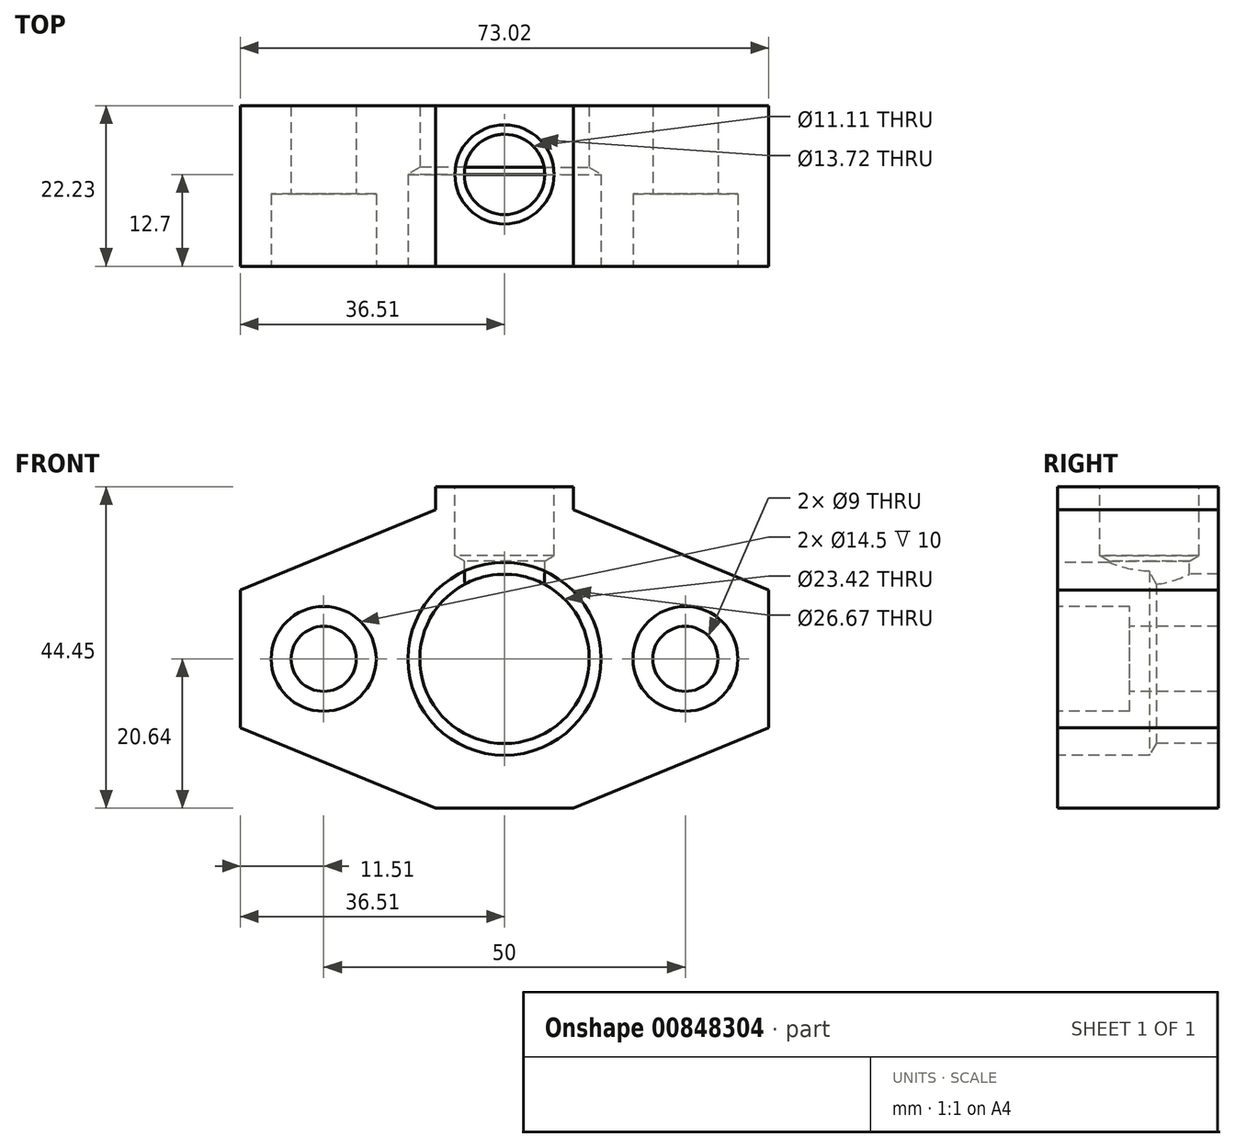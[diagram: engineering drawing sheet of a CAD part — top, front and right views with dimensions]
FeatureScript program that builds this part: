
annotation { "Feature Type Name" : "Feature", "Feature Type Description" : "" }
export const myFeature = defineFeature(function(context is Context, id is Id, definition is map)
    precondition{}
    {
        {
            var Q0;
            Q0=qCreatedBy(makeId("Front.planeOp"),FACE);
            var sketch = newSketch(context, id + "F0", { "sketchPlane" : qUnion([Q0])});
            skLineSegment(sketch, "E0", {"start": v(-36.51, 9.52) * mm, "end": v(-36.51, -9.53) * mm});
            skLineSegment(sketch, "E1", {"start": v(-36.51, -9.53) * mm, "end": v(-9.52, -20.64) * mm});
            skLineSegment(sketch, "E2", {"start": v(-9.52, -20.64) * mm, "end": v(9.52, -20.64) * mm});
            skLineSegment(sketch, "E3", {"start": v(9.52, -20.64) * mm, "end": v(36.51, -9.53) * mm});
            skLineSegment(sketch, "E4", {"start": v(36.51, -9.53) * mm, "end": v(36.51, 9.52) * mm});
            skLineSegment(sketch, "E5", {"start": v(36.51, 9.52) * mm, "end": v(9.52, 20.64) * mm});
            skLineSegment(sketch, "E6", {"start": v(9.52, 20.64) * mm, "end": v(-9.53, 20.64) * mm});
            skLineSegment(sketch, "E7", {"start": v(-9.52, 20.64) * mm, "end": v(-36.51, 9.52) * mm});
            skSolve(sketch);
        }
        {
            var Q0;
            Q0 = qSketchRegion(id + "F0", true);
            extrude(context, id + "F1", {"entities" : qUnion([Q0]), "oppositeDirection" : true, "depth" : 22.22 * mm, "offsetDistance" : 25.4 * mm});
        }
        {
            var Q0;
            Q0=makeQuery(id+"F1.opExtrude","CAP_FACE",FACE,{"disambiguationData":[OSD([sQuery(id+"F0.wireOp",EDGE,"E0"),sQuery(id+"F0.wireOp",EDGE,"E1"),sQuery(id+"F0.wireOp",EDGE,"E2"),sQuery(id+"F0.wireOp",EDGE,"E3"),sQuery(id+"F0.wireOp",EDGE,"E4"),sQuery(id+"F0.wireOp",EDGE,"E5"),sQuery(id+"F0.wireOp",EDGE,"E6"),sQuery(id+"F0.wireOp",EDGE,"E7")])],"isStart":true});
            var sketch = newSketch(context, id + "F2", { "sketchPlane" : qUnion([Q0])});
            skPoint(sketch, "E8", {"position": v(0, 0) * mm});
            skSolve(sketch);
        }
        {
            var Q0;
            Q0=sQuery(id+"F2.wireOp",VERTEX,"E8");
            var Q1;
            Q1=makeQuery(id+"F1.opExtrude","SWEPT_BODY",BODY,{"disambiguationData":[OSD([sQuery(id+"F0.wireOp",EDGE,"E0"),sQuery(id+"F0.wireOp",EDGE,"E1"),sQuery(id+"F0.wireOp",EDGE,"E2"),sQuery(id+"F0.wireOp",EDGE,"E3"),sQuery(id+"F0.wireOp",EDGE,"E4"),sQuery(id+"F0.wireOp",EDGE,"E5"),sQuery(id+"F0.wireOp",EDGE,"E6"),sQuery(id+"F0.wireOp",EDGE,"E7")])]});
            hole(context, id + "F3", {"style" : HoleStyle.SIMPLE, "endStyle" : HoleEndStyle.THROUGH, "holeDiameter" : 23.42 * mm, "majorDiameter" : 6.35 * mm, "isTappedThrough" : true, "tappedDepth" : 12.7 * mm, "tapClearance" : 3, "locations" : qUnion([Q0]), "scope" : qUnion([Q1])});
        }
        {
            var Q0;
            Q0=sQuery(id+"F2.wireOp",VERTEX,"E8");
            var Q1;
            Q1=makeQuery(id+"F1.opExtrude","SWEPT_BODY",BODY,{"disambiguationData":[OSD([sQuery(id+"F0.wireOp",EDGE,"E0"),sQuery(id+"F0.wireOp",EDGE,"E1"),sQuery(id+"F0.wireOp",EDGE,"E2"),sQuery(id+"F0.wireOp",EDGE,"E3"),sQuery(id+"F0.wireOp",EDGE,"E4"),sQuery(id+"F0.wireOp",EDGE,"E5"),sQuery(id+"F0.wireOp",EDGE,"E6"),sQuery(id+"F0.wireOp",EDGE,"E7")])]});
            hole(context, id + "F4", {"style" : HoleStyle.SIMPLE, "endStyle" : HoleEndStyle.BLIND, "holeDiameter" : 26.67 * mm, "majorDiameter" : 19.05 * mm, "holeDepth" : 12.7 * mm, "isTappedThrough" : true, "tappedDepth" : 12.7 * mm, "tapClearance" : 3, "locations" : qUnion([Q0]), "scope" : qUnion([Q1])});
        }
        {
            var Q0;
            Q0=makeQuery(id+"F1.opExtrude","SWEPT_FACE",FACE,{"disambiguationData":[OSD([sQuery(id+"F0.wireOp",EDGE,"E6")])]});
            var sketch = newSketch(context, id + "F5", { "sketchPlane" : qUnion([Q0])});
            skLineSegment(sketch, "E9.0", {"start": v(9.52, 0) * mm, "end": v(-9.53, 0) * mm});
            skLineSegment(sketch, "E10.0", {"start": v(-9.52, 22.23) * mm, "end": v(-9.52, 0) * mm});
            skLineSegment(sketch, "E11.0", {"start": v(9.52, 22.23) * mm, "end": v(-9.52, 22.23) * mm});
            skLineSegment(sketch, "E12.0", {"start": v(9.52, 22.23) * mm, "end": v(9.52, 0) * mm});
            skSolve(sketch);
        }
        {
            var Q0;
            Q0 = qSketchRegion(id + "F5", true);
            extrude(context, id + "F6", {"entities" : qUnion([Q0]), "operationType" : NewBodyOperationType.ADD, "depth" : 3.17 * mm, "offsetDistance" : 25.4 * mm});
        }
        {
            var Q0;
            Q0=makeQuery(id+"F6.opExtrude","CAP_FACE",FACE,{"disambiguationData":[OSD([sQuery(id+"F5.wireOp",EDGE,"E9.0"),sQuery(id+"F5.wireOp",EDGE,"E10.0"),sQuery(id+"F5.wireOp",EDGE,"E11.0"),sQuery(id+"F5.wireOp",EDGE,"E12.0")])],"isStart":false});
            var sketch = newSketch(context, id + "F7", { "sketchPlane" : qUnion([Q0])});
            skPoint(sketch, "E13", {"position": v(0, 12.7) * mm});
            skSolve(sketch);
        }
        {
            var Q0;
            Q0=sQuery(id+"F7.wireOp",VERTEX,"E13");
            var Q1;
            Q1=makeQuery(id+"F1.opExtrude","SWEPT_BODY",BODY,{"disambiguationData":[OSD([sQuery(id+"F0.wireOp",EDGE,"E0"),sQuery(id+"F0.wireOp",EDGE,"E1"),sQuery(id+"F0.wireOp",EDGE,"E2"),sQuery(id+"F0.wireOp",EDGE,"E3"),sQuery(id+"F0.wireOp",EDGE,"E4"),sQuery(id+"F0.wireOp",EDGE,"E5"),sQuery(id+"F0.wireOp",EDGE,"E6"),sQuery(id+"F0.wireOp",EDGE,"E7")])]});
            hole(context, id + "F8", {"style" : HoleStyle.SIMPLE, "endStyle" : HoleEndStyle.BLIND, "holeDiameter" : 11.1 * mm, "majorDiameter" : 6.35 * mm, "holeDepth" : 25.4 * mm, "isTappedThrough" : true, "tappedDepth" : 12.7 * mm, "tapClearance" : 3, "startFromSketch" : true, "locations" : qUnion([Q0]), "scope" : qUnion([Q1])});
        }
        {
            var Q0;
            Q0=sQuery(id+"F7.wireOp",VERTEX,"E13");
            var Q1;
            Q1=makeQuery(id+"F1.opExtrude","SWEPT_BODY",BODY,{"disambiguationData":[OSD([sQuery(id+"F0.wireOp",EDGE,"E0"),sQuery(id+"F0.wireOp",EDGE,"E1"),sQuery(id+"F0.wireOp",EDGE,"E2"),sQuery(id+"F0.wireOp",EDGE,"E3"),sQuery(id+"F0.wireOp",EDGE,"E4"),sQuery(id+"F0.wireOp",EDGE,"E5"),sQuery(id+"F0.wireOp",EDGE,"E6"),sQuery(id+"F0.wireOp",EDGE,"E7")])]});
            hole(context, id + "F9", {"style" : HoleStyle.SIMPLE, "endStyle" : HoleEndStyle.BLIND, "holeDiameter" : 13.72 * mm, "majorDiameter" : 6.35 * mm, "holeDepth" : 9.52 * mm, "isTappedThrough" : true, "tappedDepth" : 12.7 * mm, "tapClearance" : 3, "startFromSketch" : true, "locations" : qUnion([Q0]), "scope" : qUnion([Q1])});
        }
        {
            var Q0;
            Q0=makeQuery(id+"F6.boolean.opBoolean","MERGE",FACE,{"derivedFrom":[makeQuery(id+"F1.opExtrude","CAP_FACE",FACE,{"disambiguationData":[OSD([sQuery(id+"F0.wireOp",EDGE,"E0"),sQuery(id+"F0.wireOp",EDGE,"E1"),sQuery(id+"F0.wireOp",EDGE,"E2"),sQuery(id+"F0.wireOp",EDGE,"E3"),sQuery(id+"F0.wireOp",EDGE,"E4"),sQuery(id+"F0.wireOp",EDGE,"E5"),sQuery(id+"F0.wireOp",EDGE,"E6"),sQuery(id+"F0.wireOp",EDGE,"E7")])],"isStart":true}),makeQuery(id+"F6.opExtrude","SWEPT_FACE",FACE,{"disambiguationData":[OSD([sQuery(id+"F5.wireOp",EDGE,"E9.0")])]})]});
            var sketch = newSketch(context, id + "F10", { "sketchPlane" : qUnion([Q0])});
            skPoint(sketch, "E14", {"position": v(-25, 0) * mm});
            skPoint(sketch, "E15", {"position": v(25, 0) * mm});
            skSolve(sketch);
        }
        {
            var Q0;
            Q0=sQuery(id+"F10.wireOp",VERTEX,"E14");
            var Q1;
            Q1=sQuery(id+"F10.wireOp",VERTEX,"E15");
            var Q2;
            Q2=makeQuery(id+"F1.opExtrude","SWEPT_BODY",BODY,{"disambiguationData":[OSD([sQuery(id+"F0.wireOp",EDGE,"E0"),sQuery(id+"F0.wireOp",EDGE,"E1"),sQuery(id+"F0.wireOp",EDGE,"E2"),sQuery(id+"F0.wireOp",EDGE,"E3"),sQuery(id+"F0.wireOp",EDGE,"E4"),sQuery(id+"F0.wireOp",EDGE,"E5"),sQuery(id+"F0.wireOp",EDGE,"E6"),sQuery(id+"F0.wireOp",EDGE,"E7")])]});
            hole(context, id + "F11", {"style" : HoleStyle.C_BORE, "endStyle" : HoleEndStyle.THROUGH, "holeDiameter" : 9 * mm, "cBoreDiameter" : 14.5 * mm, "cBoreDepth" : 10 * mm, "majorDiameter" : 6.35 * mm, "isTappedThrough" : true, "tappedDepth" : 12.7 * mm, "tapClearance" : 3, "startFromSketch" : true, "locations" : qUnion([Q0, Q1]), "scope" : qUnion([Q2])});
        }
    });
